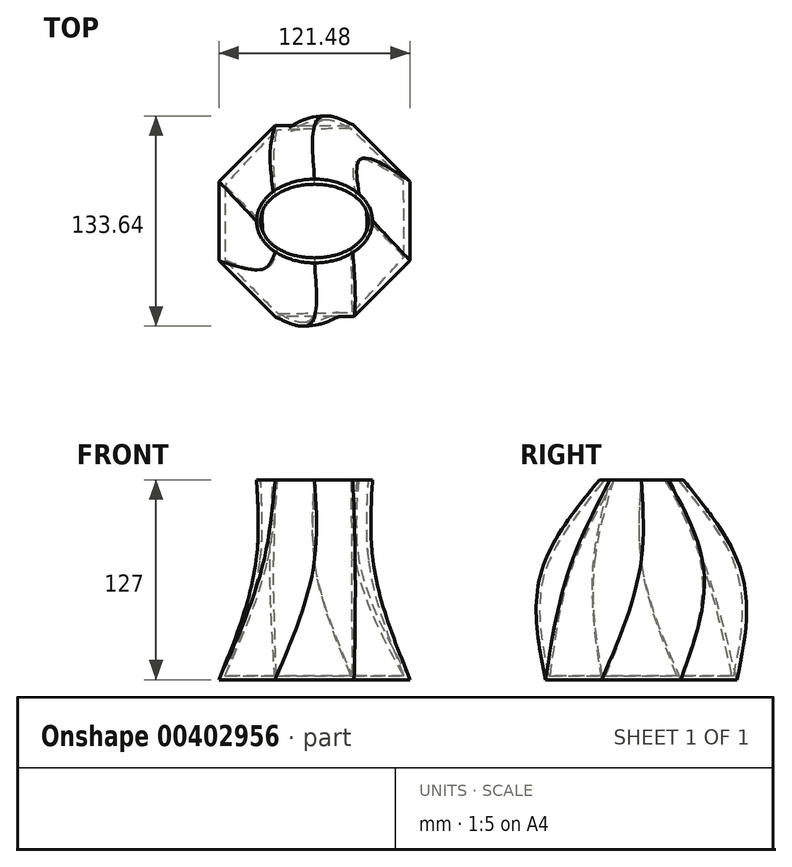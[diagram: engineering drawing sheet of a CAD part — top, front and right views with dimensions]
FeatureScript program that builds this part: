
annotation { "Feature Type Name" : "Feature", "Feature Type Description" : "" }
export const myFeature = defineFeature(function(context is Context, id is Id, definition is map)
    precondition{}
    {
        {
            var Q0;
            Q0=qCreatedBy(makeId("Top.planeOp"),FACE);
            cPlane(context, id + "F0", {"entities" : qUnion([Q0]), "cplaneType" : CPlaneType.OFFSET, "offset" : 76.2 * mm, "width" : 152.4 * mm, "height" : 152.4 * mm});
        }
        {
            var Q0;
            Q0=qCreatedBy(makeId("Top.planeOp"),FACE);
            var sketch = newSketch(context, id + "F1", { "sketchPlane" : qUnion([Q0])});
            skCircle(sketch, "E0.cCircle", {"center": v(0, 0) * mm, "radius": 60.74 * mm, "construction": true});
            skLineSegment(sketch, "E0.0", {"start": v(-60.74, -25.16) * mm, "end": v(-60.74, 25.16) * mm});
            skLineSegment(sketch, "E0.1", {"start": v(-60.74, 25.16) * mm, "end": v(-25.16, 60.74) * mm});
            skLineSegment(sketch, "E0.2", {"start": v(-25.16, 60.74) * mm, "end": v(25.16, 60.74) * mm});
            skLineSegment(sketch, "E0.3", {"start": v(25.16, 60.74) * mm, "end": v(60.74, 25.16) * mm});
            skLineSegment(sketch, "E0.4", {"start": v(60.74, 25.16) * mm, "end": v(60.74, -25.16) * mm});
            skLineSegment(sketch, "E0.5", {"start": v(60.74, -25.16) * mm, "end": v(25.16, -60.74) * mm});
            skLineSegment(sketch, "E0.6", {"start": v(25.16, -60.74) * mm, "end": v(-25.16, -60.74) * mm});
            skLineSegment(sketch, "E0.7", {"start": v(-25.16, -60.74) * mm, "end": v(-60.74, -25.16) * mm});
            skPoint(sketch, "E0.0.midPoint", {"position": v(-60.74, 0) * mm});
            skSolve(sketch);
        }
        {
            var Q0;
            Q0=qCreatedBy(id+"F0.planeOp",FACE);
            var sketch = newSketch(context, id + "F2", { "sketchPlane" : qUnion([Q0])});
            skEllipticalArc(sketch, "E1", {});
            skEllipticalArc(sketch, "E2", {});
            skEllipticalArc(sketch, "E3", {});
            skEllipticalArc(sketch, "E4", {});
            skEllipticalArc(sketch, "E5", {});
            skEllipticalArc(sketch, "E6", {});
            skEllipticalArc(sketch, "E7", {});
            skEllipticalArc(sketch, "E8", {});
            const initialGuessF2  = {"E1": [0, 0, 0, 1, 0.06087139621376991, 0.03700223580260315, 0, 0.8683856319752135], "E2": [0, 0, 0, 1, 0.06087139621376991, 0.03700223580260315, 4.71238898038469, 5.403269404012432], "E3": [0, 0, 0, 1, 0.06087139621376991, 0.03700223580260315, 3.141592653589793, 3.911830107253981], "E4": [0, 0, 0, 1, 0.06087139621376991, 0.03700223580260315, 1.5707963267948966, 2.0907977020312383], "E5": [0, 0, 0, 1, 0.06087139621376991, 0.03700223580260315, 0.8683856319752135, 1.5707963267948966], "E6": [0, 0, 0, 1, 0.06087139621376991, 0.03700223580260315, 3.911830107253981, 4.71238898038469], "E7": [0, 0, 0, 1, 0.06087139621376991, 0.03700223580260315, 5.403269404012432, 0], "E8": [0, 0, 0, 1, 0.06087139621376991, 0.03700223580260315, 2.0907977020312383, 3.141592653589793]};
            skSetInitialGuess(sketch, initialGuessF2);
            skSolve(sketch);
        }
        {
            var Q0;
            Q0=qCreatedBy(id+"F0.planeOp",FACE);
            cPlane(context, id + "F3", {"entities" : qUnion([Q0]), "cplaneType" : CPlaneType.OFFSET, "offset" : 50.8 * mm, "width" : 152.4 * mm, "height" : 152.4 * mm});
        }
        {
            var Q0;
            Q0=qCreatedBy(id+"F3.planeOp",FACE);
            var sketch = newSketch(context, id + "F4", { "sketchPlane" : qUnion([Q0])});
            skEllipticalArc(sketch, "E9", {});
            skEllipticalArc(sketch, "E10", {});
            skEllipticalArc(sketch, "E11", {});
            skEllipticalArc(sketch, "E12", {});
            skEllipticalArc(sketch, "E13", {});
            skEllipticalArc(sketch, "E14", {});
            skEllipticalArc(sketch, "E15", {});
            skEllipticalArc(sketch, "E16", {});
            const initialGuessF4  = {"E9": [0, 0, 1, 0, 0.036815233528614044, 0.02661028332637567, 4.71238898038469, 5.43659923887018], "E10": [0, 0, 1, 0, 0.036815233528614044, 0.02661028332637567, 1.5707963267948966, 2.366950804434332], "E11": [0, 0, 1, 0, 0.036815233528614044, 0.02661028332637567, 3.141592653589793, 3.9675414735876564], "E12": [0, 0, 1, 0, 0.036815233528614044, 0.02661028332637567, 0, 0.6946762010906652], "E13": [0, 0, 1, 0, 0.036815233528614044, 0.02661028332637567, 5.43659923887018, 0], "E14": [0, 0, 1, 0, 0.036815233528614044, 0.02661028332637567, 2.366950804434332, 3.141592653589793], "E15": [0, 0, 1, 0, 0.036815233528614044, 0.02661028332637567, 0.6946762010906653, 1.5707963267948966], "E16": [0, 0, 1, 0, 0.036815233528614044, 0.02661028332637567, 3.9675414735876564, 4.71238898038469]};
            skSetInitialGuess(sketch, initialGuessF4);
            skSolve(sketch);
        }
        {
            var Q0;
            Q0=makeQuery(id+"F1.imprint","IMPRINT",FACE,{"disambiguationData":[TD([[makeQuery(id+"F1.imprint","IMPRINT",EDGE,{"derivedFrom":sQuery(id+"F1.wireOp",EDGE,"E0.0")}),-1.0]])]});
            var Q1;
            Q1=makeQuery(id+"F2.imprint","IMPRINT",FACE,{"disambiguationData":[TD([[makeQuery(id+"F2.imprint","IMPRINT",EDGE,{"derivedFrom":sQuery(id+"F2.wireOp",EDGE,"E1")}),1.0]])]});
            var Q2;
            Q2=makeQuery(id+"F4.imprint","IMPRINT",FACE,{"disambiguationData":[TD([[makeQuery(id+"F4.imprint","IMPRINT",EDGE,{"derivedFrom":sQuery(id+"F4.wireOp",EDGE,"E9")}),1.0]])]});
            loft(context, id + "F5", {"sheetProfilesArray" : [{ "sheetProfileEntities" : qUnion([Q0]) }, { "sheetProfileEntities" : qUnion([Q1]) }, { "sheetProfileEntities" : qUnion([Q2]) }]});
        }
        {
            var Q0;
            Q0=makeQuery(id+"F5.opLoft","CAP_FACE",FACE,{"disambiguationData":[OSD([makeQuery(id+"F4.imprint","IMPRINT",FACE,{"disambiguationData":[TD([[makeQuery(id+"F4.imprint","IMPRINT",EDGE,{"derivedFrom":sQuery(id+"F4.wireOp",EDGE,"E9")}),1.0]])]})])],"isStart":true});
            shell(context, id + "F6", {"entities" : qUnion([Q0]), "thickness" : 2.54 * mm});
        }
    });
